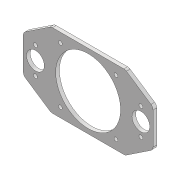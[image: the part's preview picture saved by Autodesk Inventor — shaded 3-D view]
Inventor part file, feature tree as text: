
AUTODESK INVENTOR PART (.ipt)
format: ipt  version: 2020 (Build 240168000, 168)  size: 175,616 bytes
history: native  units: mm
features: other x4, mirror x2, extrude x1, fillet x1, sketch x1
ambient origin geometry x8: Origin, YZ Plane, XZ Plane, XY Plane, X Axis, Y Axis, Z Axis, Center Point
bodies: Body1 (feature_tree)
feature tree (9):
  other  "Plano de trabalho1"
  extrude  "Extrusão2"  Depth=4.0mm
  mirror  "Espelhamento1"
  mirror  "Espelhamento2"
  fillet  "Arredondamento1"  Radius=4.0mm
  sketch  "Esboço1"  dims[d0=70.0mm d3=4.0mm d4=4.0mm d5=4.0mm d6=4.0mm d7=19.2mm d8=30.0mm d9=20.0mm d10=4.0mm d11=0.0mm d12=4.2mm d13=14.5mm d14=16.87302mm d15=16.87302mm d16=5.0mm]
  other  "<userpath>\OneDrive\Área de Trabalho\Calorimetro 2022\Inventor\parte_superior.iam"
  other  "parte_superior.iam"
  other  "Corpo_1:4"
